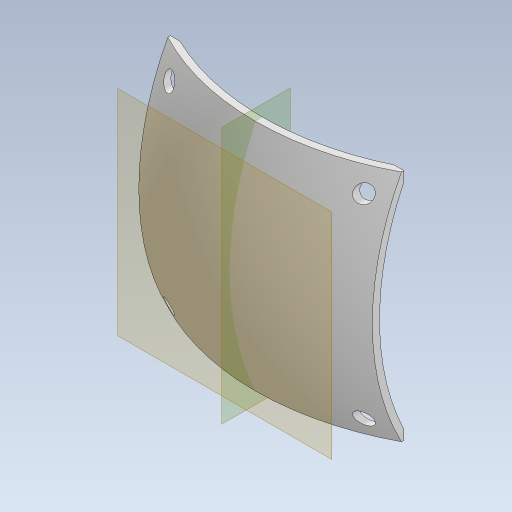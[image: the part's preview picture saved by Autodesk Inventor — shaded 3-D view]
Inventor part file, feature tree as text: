
AUTODESK INVENTOR PART (.ipt)
format: ipt  version: 2023 (Build 270158030, 158C)  size: 224,768 bytes
history: native  units: mm
features: other x5, sketch x3, reference x3, plane x2, extrude x2, revolve x1, projected_geometry x1
ambient origin geometry x8: Origin, YZ Plane, XZ Plane, XY Plane, X Axis, Y Axis, Z Axis, Center Point
bodies: Body1 (feature_tree)
feature tree (17):
  other  "sling"
  plane  "Work Plane1"
  extrude  "Extrusion1"  Depth=30.0mm
  plane  "Work Plane2"
  revolve  "Revolution1"  [1 undecoded]
  extrude  "Extrusion2"  Depth=1.0mm TaperAngle=0.0deg
  sketch  "Sketch1"  dims[d0=30.0mm d1=30.0mm]
  reference  "Reference1"
  reference  "Reference2"
  reference  "Reference3"
  sketch  "Sketch2"  dims[d2=15.0mm d3=12.5mm]
  projected_geometry  "Projected Loop1"
  sketch  "Sketch3"  dims[d4=12.5mm d5=8.0mm d6=0.0mm d7=360.0deg d9=15.0mm d19=15.0mm d20=11.0mm d21=11.0mm d22=4.0mm d23=1.0mm d24=2.0mm d25=2.5mm d26=2.5mm d27=2.5mm d28=2.5mm d29=0.0mm d30=0.0mm]
  other  "<userpath>\Documents\0004-inventor\3D-CAD-main\trebuchet\trebuchet-assembly.iam"
  other  "trebuchet-assembly.iam"
  other  "V1_baseplate:1"
  other  "bolder:1"
note: 1 required parameter value undecoded (feature->parameter linkage not recoverable at this tier; creation-order binding heuristic only, values carry confidence <= 0.55)
